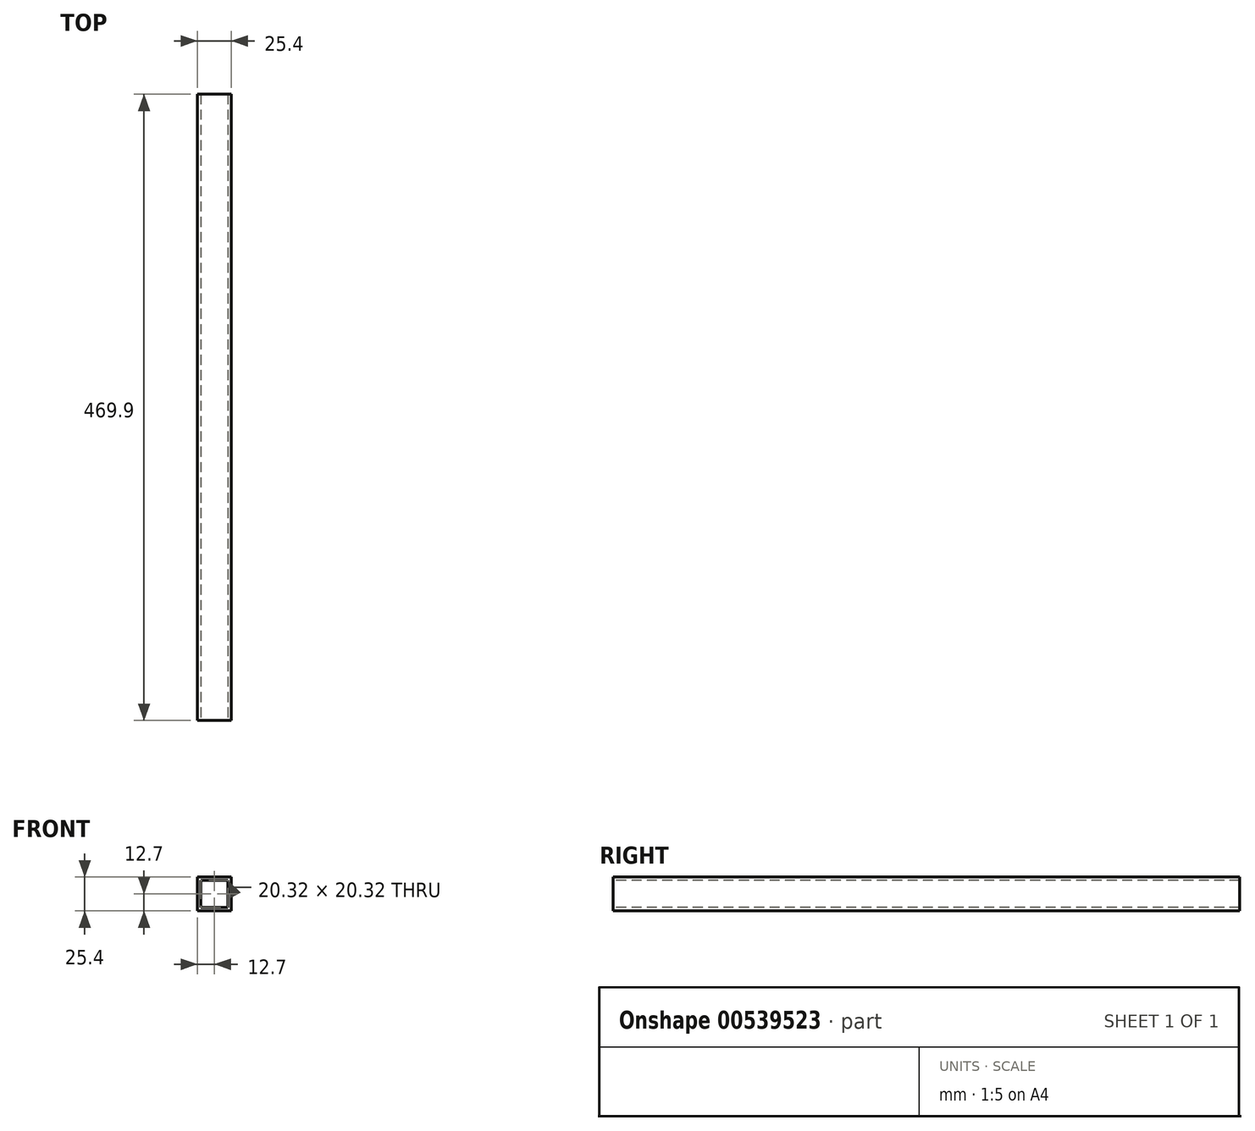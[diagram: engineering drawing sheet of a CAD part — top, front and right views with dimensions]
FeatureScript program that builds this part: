
annotation { "Feature Type Name" : "Feature", "Feature Type Description" : "" }
export const myFeature = defineFeature(function(context is Context, id is Id, definition is map)
    precondition{}
    {
        {
            var Q0;
            Q0=qCreatedBy(makeId("Front.planeOp"),FACE);
            var sketch = newSketch(context, id + "F0", { "sketchPlane" : qUnion([Q0])});
            skLineSegment(sketch, "E0.bottom", {"start": v(12.7, -12.7) * mm, "end": v(-12.7, -12.7) * mm});
            skLineSegment(sketch, "E0.top", {"start": v(12.7, 12.7) * mm, "end": v(-12.7, 12.7) * mm});
            skLineSegment(sketch, "E0.left", {"start": v(12.7, -12.7) * mm, "end": v(12.7, 12.7) * mm});
            skLineSegment(sketch, "E0.right", {"start": v(-12.7, -12.7) * mm, "end": v(-12.7, 12.7) * mm});
            skPoint(sketch, "E0.middle", {"position": v(0, 0) * mm});
            skSolve(sketch);
        }
        {
            var Q0;
            Q0=makeQuery(id+"F0.imprint","IMPRINT",FACE,{"disambiguationData":[TD([[makeQuery(id+"F0.imprint","IMPRINT",EDGE,{"derivedFrom":sQuery(id+"F0.wireOp",EDGE,"E0.bottom")}),-1.0]])]});
            extrude(context, id + "F1", {"entities" : qUnion([Q0]), "depth" : 469.9 * mm, "offsetDistance" : 25.4 * mm});
        }
        {
            var Q0;
            Q0=makeQuery(id+"F1.opExtrude","CAP_FACE",FACE,{"disambiguationData":[OSD([sQuery(id+"F0.wireOp",EDGE,"E0.bottom"),sQuery(id+"F0.wireOp",EDGE,"E0.top"),sQuery(id+"F0.wireOp",EDGE,"E0.left"),sQuery(id+"F0.wireOp",EDGE,"E0.right")])],"isStart":false});
            var sketch = newSketch(context, id + "F2", { "sketchPlane" : qUnion([Q0])});
            skLineSegment(sketch, "E1.bottom", {"start": v(10.16, -10.16) * mm, "end": v(-10.16, -10.16) * mm});
            skLineSegment(sketch, "E1.top", {"start": v(10.16, 10.16) * mm, "end": v(-10.16, 10.16) * mm});
            skLineSegment(sketch, "E1.left", {"start": v(10.16, -10.16) * mm, "end": v(10.16, 10.16) * mm});
            skLineSegment(sketch, "E1.right", {"start": v(-10.16, -10.16) * mm, "end": v(-10.16, 10.16) * mm});
            skPoint(sketch, "E1.middle", {"position": v(0, 0) * mm});
            skSolve(sketch);
        }
        {
            var Q0;
            Q0=makeQuery(id+"F2.imprint","IMPRINT",FACE,{"disambiguationData":[TD([[makeQuery(id+"F2.imprint","IMPRINT",EDGE,{"derivedFrom":sQuery(id+"F2.wireOp",EDGE,"E1.bottom")}),-1.0]])]});
            extrude(context, id + "F3", {"entities" : qUnion([Q0]), "operationType" : NewBodyOperationType.REMOVE, "endBound" : BoundingType.THROUGH_ALL, "oppositeDirection" : true, "depth" : 25.4 * mm, "offsetDistance" : 25.4 * mm});
        }
    });
